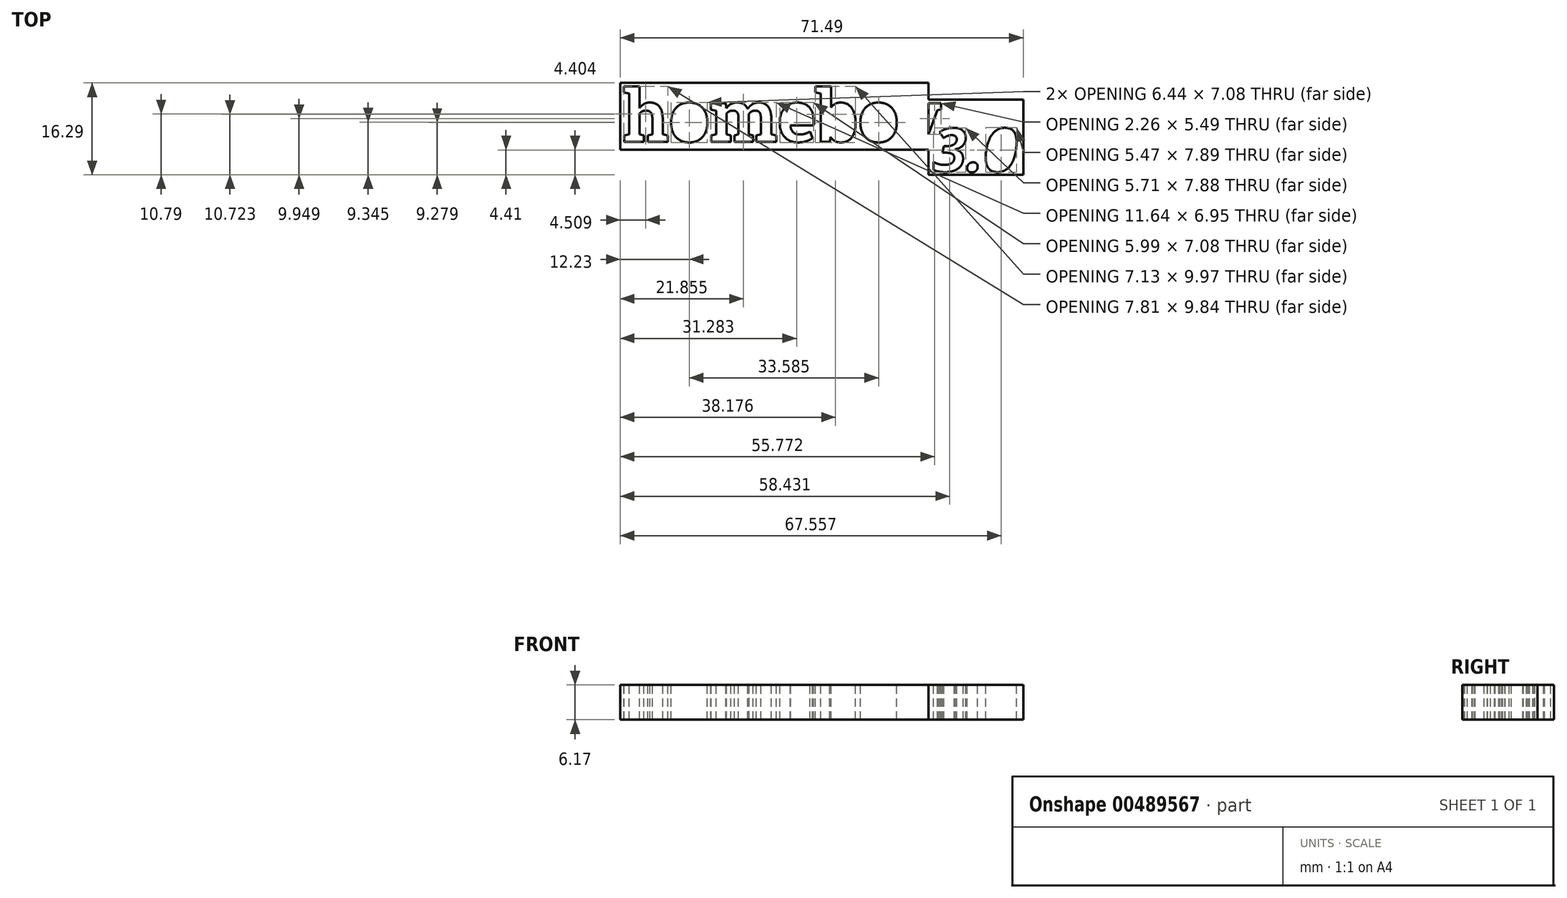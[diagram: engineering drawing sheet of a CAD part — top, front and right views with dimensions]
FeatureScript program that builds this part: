
annotation { "Feature Type Name" : "Feature", "Feature Type Description" : "" }
export const myFeature = defineFeature(function(context is Context, id is Id, definition is map)
    precondition{}
    {
        {
            var Q0;
            Q0=qCreatedBy(makeId("Top.planeOp"),FACE);
            var sketch = newSketch(context, id + "F0", { "sketchPlane" : qUnion([Q0])});
            skText(sketch, "E0", { "text": "homeboy", "fontName": "RobotoSlab-Bold.ttf"});
            skText(sketch, "E1", { "text": "3.0", "fontName": "NotoSans-BoldItalic.ttf"});
            skPoint(sketch, "E2.oppositeSnap0", {"position": v(1.43, 4.44) * mm});
            skLineSegment(sketch, "E2.bottom", {"start": v(-54.07, 16.3) * mm, "end": v(0.57, 16.3) * mm});
            skLineSegment(sketch, "E2.top", {"start": v(-54.07, 4.44) * mm, "end": v(0.57, 4.44) * mm});
            skLineSegment(sketch, "E2.left", {"start": v(-54.07, 16.3) * mm, "end": v(-54.07, 4.44) * mm});
            skLineSegment(sketch, "E2.right", {"start": v(0.57, 16.3) * mm, "end": v(0.57, 4.44) * mm});
            skLineSegment(sketch, "E3.bottom", {"start": v(0.57, 13.35) * mm, "end": v(17.42, 13.35) * mm});
            skLineSegment(sketch, "E3.top", {"start": v(0.57, 0) * mm, "end": v(17.42, 0) * mm});
            skLineSegment(sketch, "E3.left", {"start": v(0.57, 13.35) * mm, "end": v(0.57, 0) * mm});
            skLineSegment(sketch, "E3.right", {"start": v(17.42, 13.35) * mm, "end": v(17.42, 0) * mm});
            const initialGuessF0  = {"E0": [-0.05367, 0.00587, 1, 0, 0.0093], "E1": [0.00143, 0.00057, 1, 0, 0.00773]};
            skSetInitialGuess(sketch, initialGuessF0);
            skSolve(sketch);
        }
        {
            var Q0;
            {var subQ0=sQuery(id+"F0.wireOp",EDGE,"E0.sketch_text.stroke-161");var subQ1=sQuery(id+"F0.wireOp",EDGE,"E0.sketch_text.stroke-160");var subQ2=makeQuery(id+"F0.imprint","INTERSECT",VERTEX,{"derivedFrom":[subQ1,subQ0]});Q0=makeQuery(id+"F0.imprint","IMPRINT",FACE,{"disambiguationData":[TD([[makeQuery(id+"F0.imprint","IMPRINT",EDGE,{"disambiguationData":[TD([[subQ2,1.0]])],"derivedFrom":subQ1}),1.0]])]});}
            var Q1;
            {var subQ9=sQuery(id+"F0.wireOp",EDGE,"E0.sketch_text.stroke-166");Q1=makeQuery(id+"F0.imprint","IMPRINT",FACE,{"disambiguationData":[TD([[makeQuery(id+"F0.imprint","IMPRINT",EDGE,{"derivedFrom":subQ9}),-1.0]])]});}
            var Q2;
            {var subQ1=sQuery(id+"F0.wireOp",EDGE,"E0.sketch_text.stroke-159");Q2=makeQuery(id+"F0.imprint","IMPRINT",FACE,{"disambiguationData":[TD([[makeQuery(id+"F0.imprint","IMPRINT",EDGE,{"derivedFrom":subQ1}),1.0]])]});}
            var Q3;
            Q3=makeQuery(id+"F0.imprint","IMPRINT",FACE,{"disambiguationData":[TD([[makeQuery(id+"F0.imprint","IMPRINT",EDGE,{"derivedFrom":sQuery(id+"F0.wireOp",EDGE,"E0.sketch_text.stroke-0")}),1.0]])]});
            extrude(context, id + "F1", {"entities" : qUnion([Q0, Q1, Q2, Q3]), "oppositeDirection" : true, "depth" : 6.17 * mm});
        }
    });
